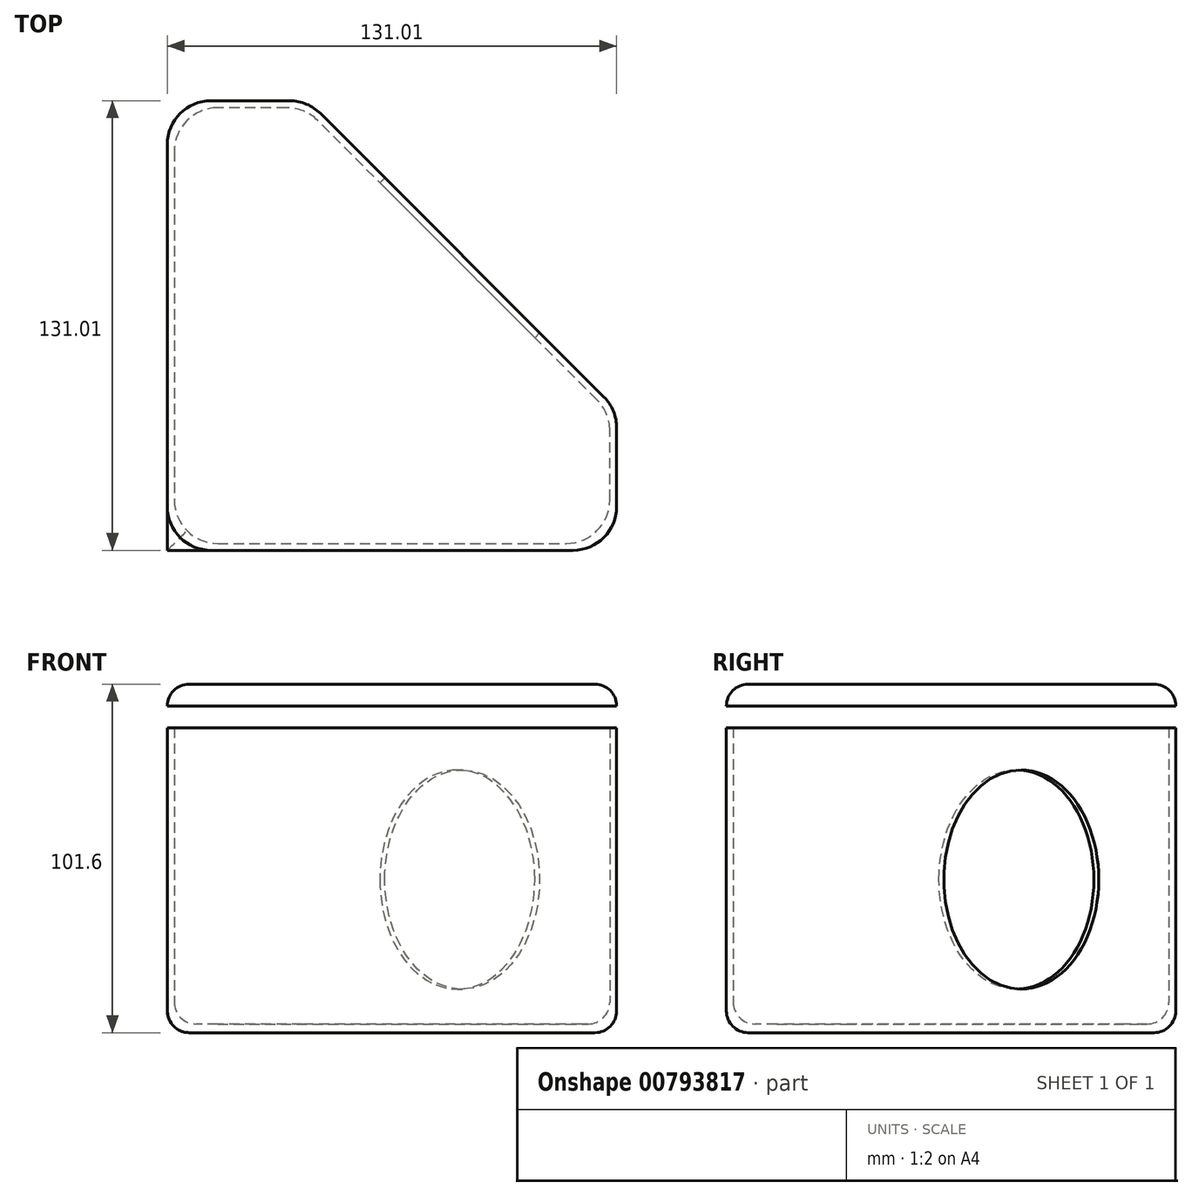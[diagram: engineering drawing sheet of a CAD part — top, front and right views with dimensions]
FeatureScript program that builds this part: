
annotation { "Feature Type Name" : "Feature", "Feature Type Description" : "" }
export const myFeature = defineFeature(function(context is Context, id is Id, definition is map)
    precondition{}
    {
        {
            var Q0;
            Q0=qCreatedBy(makeId("Top.planeOp"),FACE);
            var sketch = newSketch(context, id + "F0", { "sketchPlane" : qUnion([Q0])});
            skLineSegment(sketch, "E0", {"start": v(-131, 131) * mm, "end": v(-131, 0) * mm});
            skLineSegment(sketch, "E1", {"start": v(-131, 0) * mm, "end": v(0, 0) * mm});
            skLineSegment(sketch, "E2", {"start": v(0, 0) * mm, "end": v(0, 40.93) * mm});
            skLineSegment(sketch, "E3", {"start": v(0, 40.93) * mm, "end": v(-90.07, 131) * mm});
            skLineSegment(sketch, "E4", {"start": v(-90.07, 131) * mm, "end": v(-131, 131) * mm});
            skLineSegment(sketch, "E5.0", {"start": v(-129, 129) * mm, "end": v(-129, 2) * mm});
            skLineSegment(sketch, "E5.1", {"start": v(-90.9, 129) * mm, "end": v(-129, 129) * mm});
            skLineSegment(sketch, "E5.2", {"start": v(-129, 2) * mm, "end": v(-2, 2) * mm});
            skLineSegment(sketch, "E5.3", {"start": v(-2, 2) * mm, "end": v(-2, 40.1) * mm});
            skLineSegment(sketch, "E5.4", {"start": v(-2, 40.1) * mm, "end": v(-90.9, 129) * mm});
            skSolve(sketch);
        }
        {
            var Q0;
            Q0=qCreatedBy(makeId("Top.planeOp"),FACE);
            cPlane(context, id + "F1", {"entities" : qUnion([Q0]), "cplaneType" : CPlaneType.OFFSET, "offset" : 101.6 * mm, "width" : 152.4 * mm, "height" : 152.4 * mm});
        }
        {
            var Q0;
            Q0=qCreatedBy(id+"F1.planeOp",FACE);
            var sketch = newSketch(context, id + "F2", { "sketchPlane" : qUnion([Q0])});
            skLineSegment(sketch, "E6", {"start": v(0, 0) * mm, "end": v(-131.01, 0) * mm});
            skLineSegment(sketch, "E7", {"start": v(-131.01, 0) * mm, "end": v(-131.01, 131.01) * mm});
            skLineSegment(sketch, "E8", {"start": v(-131.01, 131.01) * mm, "end": v(-90.08, 131.01) * mm});
            skLineSegment(sketch, "E9", {"start": v(-90.08, 131.01) * mm, "end": v(0, 40.94) * mm});
            skLineSegment(sketch, "E10", {"start": v(0, 40.94) * mm, "end": v(0, 0) * mm});
            skLineSegment(sketch, "E11.0", {"start": v(-129, 129) * mm, "end": v(-90.9, 129) * mm});
            skLineSegment(sketch, "E11.1", {"start": v(-129, 2) * mm, "end": v(-129, 129) * mm});
            skLineSegment(sketch, "E11.2", {"start": v(-90.9, 129) * mm, "end": v(-2, 40.1) * mm});
            skLineSegment(sketch, "E11.3", {"start": v(-2, 40.1) * mm, "end": v(-2, 2) * mm});
            skLineSegment(sketch, "E11.4", {"start": v(-2, 2) * mm, "end": v(-129, 2) * mm});
            skLineSegment(sketch, "E12", {"start": v(-129, 2) * mm, "end": v(-131.01, 0) * mm});
            skLineSegment(sketch, "E13", {"start": v(-129, 129) * mm, "end": v(-131.01, 131.01) * mm});
            skLineSegment(sketch, "E14", {"start": v(-90.08, 131.01) * mm, "end": v(-90.9, 129) * mm});
            skLineSegment(sketch, "E15", {"start": v(-2, 40.1) * mm, "end": v(0, 40.94) * mm});
            skLineSegment(sketch, "E16", {"start": v(-2, 2) * mm, "end": v(0, 0) * mm});
            skSolve(sketch);
        }
        {
            var Q0;
            Q0=makeQuery(id+"F2.imprint","IMPRINT",FACE,{"disambiguationData":[TD([[makeQuery(id+"F2.imprint","IMPRINT",EDGE,{"derivedFrom":sQuery(id+"F2.wireOp",EDGE,"E11.0")}),-1.0]])]});
            var Q1;
            Q1=makeQuery(id+"F2.imprint","IMPRINT",FACE,{"disambiguationData":[TD([[makeQuery(id+"F2.imprint","IMPRINT",EDGE,{"derivedFrom":sQuery(id+"F2.wireOp",EDGE,"E10")}),-1.0]])]});
            var Q2;
            Q2=makeQuery(id+"F2.imprint","IMPRINT",FACE,{"disambiguationData":[TD([[makeQuery(id+"F2.imprint","IMPRINT",EDGE,{"derivedFrom":sQuery(id+"F2.wireOp",EDGE,"E8")}),-1.0]])]});
            var Q3;
            Q3=makeQuery(id+"F2.imprint","IMPRINT",FACE,{"disambiguationData":[TD([[makeQuery(id+"F2.imprint","IMPRINT",EDGE,{"derivedFrom":sQuery(id+"F2.wireOp",EDGE,"E9")}),-1.0]])]});
            var Q4;
            Q4=makeQuery(id+"F2.imprint","IMPRINT",FACE,{"disambiguationData":[TD([[makeQuery(id+"F2.imprint","IMPRINT",EDGE,{"derivedFrom":sQuery(id+"F2.wireOp",EDGE,"E6")}),-1.0]])]});
            var Q5;
            Q5=makeQuery(id+"F2.imprint","IMPRINT",FACE,{"disambiguationData":[TD([[makeQuery(id+"F2.imprint","IMPRINT",EDGE,{"derivedFrom":sQuery(id+"F2.wireOp",EDGE,"E7")}),-1.0]])]});
            extrude(context, id + "F3", {"entities" : qUnion([Q0, Q1, Q2, Q3, Q4, Q5]), "depth" : -6.35 * mm, "offsetDistance" : 25.4 * mm});
        }
        {
            var Q0;
            Q0=makeQuery(id+"F0.imprint","IMPRINT",FACE,{"disambiguationData":[TD([[makeQuery(id+"F0.imprint","IMPRINT",EDGE,{"derivedFrom":sQuery(id+"F0.wireOp",EDGE,"E0")}),1.0]])]});
            extrude(context, id + "F4", {"entities" : qUnion([Q0]), "operationType" : NewBodyOperationType.ADD, "depth" : 88.9 * mm, "offsetDistance" : 25.4 * mm});
        }
        {
            var Q0;
            Q0=makeQuery(id+"F0.imprint","IMPRINT",FACE,{"disambiguationData":[TD([[makeQuery(id+"F0.imprint","IMPRINT",EDGE,{"derivedFrom":sQuery(id+"F0.wireOp",EDGE,"E5.0")}),1.0]])]});
            extrude(context, id + "F5", {"entities" : qUnion([Q0]), "operationType" : NewBodyOperationType.ADD, "depth" : 2.54 * mm, "offsetDistance" : 25.4 * mm});
        }
        {
            var Q0;
            Q0=makeQuery(id+"F4.opExtrude","SWEPT_FACE",FACE,{"disambiguationData":[OSD([sQuery(id+"F0.wireOp",EDGE,"E3")])]});
            var sketch = newSketch(context, id + "F6", { "sketchPlane" : qUnion([Q0])});
            skCircle(sketch, "E17", {"center": v(92.63, 44.64) * mm, "radius": 31.94 * mm});
            skSolve(sketch);
        }
        {
            var Q0;
            Q0 = qSketchRegion(id + "F6", true);
            extrude(context, id + "F7", {"entities" : qUnion([Q0]), "operationType" : NewBodyOperationType.REMOVE, "oppositeDirection" : true, "depth" : 25.4 * mm, "offsetDistance" : 25.4 * mm});
        }
        {
            var Q0;
            Q0=makeQuery(id+"F4.opExtrude","SWEPT_EDGE",EDGE,{"disambiguationData":[OSD([sQuery(id+"F0.wireOp",EDGE,"E2"),sQuery(id+"F0.wireOp",EDGE,"E3")])]});
            var Q1;
            Q1=makeQuery(id+"F4.opExtrude","SWEPT_EDGE",EDGE,{"disambiguationData":[OSD([sQuery(id+"F0.wireOp",EDGE,"E1"),sQuery(id+"F0.wireOp",EDGE,"E2")])]});
            var Q2;
            Q2=makeQuery(id+"F4.opExtrude","SWEPT_EDGE",EDGE,{"disambiguationData":[OSD([sQuery(id+"F0.wireOp",EDGE,"E3"),sQuery(id+"F0.wireOp",EDGE,"E4")])]});
            var Q3;
            Q3=makeQuery(id+"F4.opExtrude","SWEPT_EDGE",EDGE,{"disambiguationData":[OSD([sQuery(id+"F0.wireOp",EDGE,"E0"),sQuery(id+"F0.wireOp",EDGE,"E4")])]});
            var Q4;
            Q4=makeQuery(id+"F4.opExtrude","SWEPT_EDGE",EDGE,{"disambiguationData":[OSD([sQuery(id+"F0.wireOp",EDGE,"E5.0"),sQuery(id+"F0.wireOp",EDGE,"E5.2")])]});
            var Q5;
            Q5=makeQuery(id+"F4.opExtrude","SWEPT_EDGE",EDGE,{"disambiguationData":[OSD([sQuery(id+"F0.wireOp",EDGE,"E5.2"),sQuery(id+"F0.wireOp",EDGE,"E5.3")])]});
            var Q6;
            Q6=makeQuery(id+"F4.opExtrude","SWEPT_EDGE",EDGE,{"disambiguationData":[OSD([sQuery(id+"F0.wireOp",EDGE,"E5.3"),sQuery(id+"F0.wireOp",EDGE,"E5.4")])]});
            var Q7;
            Q7=makeQuery(id+"F4.opExtrude","SWEPT_EDGE",EDGE,{"disambiguationData":[OSD([sQuery(id+"F0.wireOp",EDGE,"E5.1"),sQuery(id+"F0.wireOp",EDGE,"E5.4")])]});
            var Q8;
            Q8=makeQuery(id+"F4.opExtrude","SWEPT_EDGE",EDGE,{"disambiguationData":[OSD([sQuery(id+"F0.wireOp",EDGE,"E5.0"),sQuery(id+"F0.wireOp",EDGE,"E5.1")])]});
            fillet(context, id + "F8", {"entities" : qUnion([Q0, Q1, Q2, Q3, Q4, Q5, Q6, Q7, Q8]), "radius" : 12.7 * mm, "tangentPropagation" : true, "allowEdgeOverflow" : false});
        }
        {
            var Q0;
            Q0=makeQuery(id+"F3.opExtrude","SWEPT_EDGE",EDGE,{"disambiguationData":[OSD([sQuery(id+"F2.wireOp",EDGE,"E9"),sQuery(id+"F2.wireOp",EDGE,"E10"),sQuery(id+"F2.wireOp",EDGE,"E15")])]});
            var Q1;
            Q1=makeQuery(id+"F3.opExtrude","SWEPT_EDGE",EDGE,{"disambiguationData":[OSD([sQuery(id+"F2.wireOp",EDGE,"E8"),sQuery(id+"F2.wireOp",EDGE,"E9"),sQuery(id+"F2.wireOp",EDGE,"E14")])]});
            var Q2;
            Q2=makeQuery(id+"F3.opExtrude","SWEPT_EDGE",EDGE,{"disambiguationData":[OSD([sQuery(id+"F2.wireOp",EDGE,"E7"),sQuery(id+"F2.wireOp",EDGE,"E8"),sQuery(id+"F2.wireOp",EDGE,"E13")])]});
            var Q3;
            Q3=makeQuery(id+"F3.opExtrude","SWEPT_EDGE",EDGE,{"disambiguationData":[OSD([sQuery(id+"F2.wireOp",EDGE,"E6"),sQuery(id+"F2.wireOp",EDGE,"E7"),sQuery(id+"F2.wireOp",EDGE,"E12")])]});
            var Q4;
            Q4=makeQuery(id+"F3.opExtrude","SWEPT_EDGE",EDGE,{"disambiguationData":[OSD([sQuery(id+"F2.wireOp",EDGE,"E6"),sQuery(id+"F2.wireOp",EDGE,"E10"),sQuery(id+"F2.wireOp",EDGE,"E16")])]});
            fillet(context, id + "F9", {"entities" : qUnion([Q0, Q1, Q2, Q3, Q4]), "radius" : 12.7 * mm, "tangentPropagation" : true, "allowEdgeOverflow" : false});
        }
        {
            var Q0;
            Q0=makeQuery(id+"F3.opExtrude","CAP_FACE",FACE,{"disambiguationData":[OSD([sQuery(id+"F2.wireOp",EDGE,"E6"),sQuery(id+"F2.wireOp",EDGE,"E7"),sQuery(id+"F2.wireOp",EDGE,"E8"),sQuery(id+"F2.wireOp",EDGE,"E9"),sQuery(id+"F2.wireOp",EDGE,"E10")])],"isStart":true});
            fillet(context, id + "F10", {"entities" : qUnion([Q0]), "radius" : 6.35 * mm, "tangentPropagation" : true, "allowEdgeOverflow" : false});
        }
        {
            var Q0;
            Q0=makeQuery(id+"F5.opExtrude","CAP_FACE",FACE,{"disambiguationData":[OSD([sQuery(id+"F0.wireOp",EDGE,"E5.0"),sQuery(id+"F0.wireOp",EDGE,"E5.1"),sQuery(id+"F0.wireOp",EDGE,"E5.2"),sQuery(id+"F0.wireOp",EDGE,"E5.3"),sQuery(id+"F0.wireOp",EDGE,"E5.4")])],"isStart":false});
            var Q1;
            {var subQ0=sQuery(id+"F0.wireOp",EDGE,"E5.4");var subQ1=sQuery(id+"F0.wireOp",EDGE,"E5.3");var subQ2=sQuery(id+"F0.wireOp",EDGE,"E5.2");var subQ3=sQuery(id+"F0.wireOp",EDGE,"E5.1");var subQ4=sQuery(id+"F0.wireOp",EDGE,"E5.0");Q1=makeQuery(id+"F5.boolean.opBoolean","MERGE",FACE,{"derivedFrom":[makeQuery(id+"F4.opExtrude","CAP_FACE",FACE,{"disambiguationData":[OSD([sQuery(id+"F0.wireOp",EDGE,"E0"),sQuery(id+"F0.wireOp",EDGE,"E1"),sQuery(id+"F0.wireOp",EDGE,"E2"),sQuery(id+"F0.wireOp",EDGE,"E3"),sQuery(id+"F0.wireOp",EDGE,"E4"),subQ4,subQ3,subQ2,subQ1,subQ0])],"isStart":true}),makeQuery(id+"F5.opExtrude","CAP_FACE",FACE,{"disambiguationData":[OSD([subQ4,subQ3,subQ2,subQ1,subQ0])],"isStart":true})]});}
            fillet(context, id + "F11", {"entities" : qUnion([Q0, Q1]), "radius" : 6.35 * mm, "tangentPropagation" : true, "allowEdgeOverflow" : false});
        }
    });
